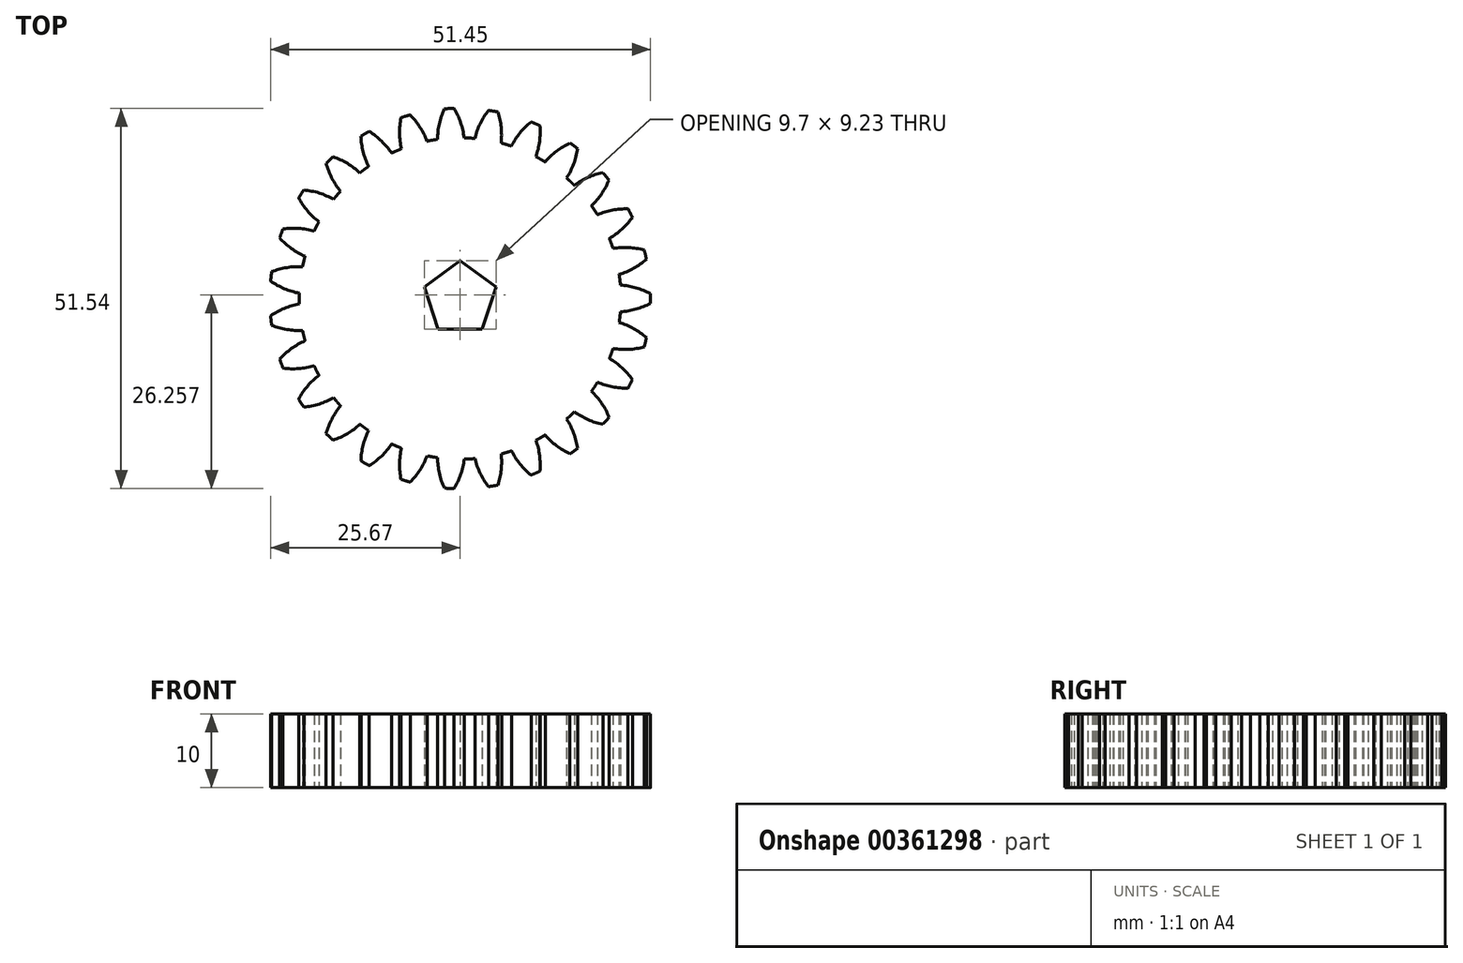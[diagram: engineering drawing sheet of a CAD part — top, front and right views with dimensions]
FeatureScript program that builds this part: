
annotation { "Feature Type Name" : "Feature", "Feature Type Description" : "" }
export const myFeature = defineFeature(function(context is Context, id is Id, definition is map)
    precondition{}
    {
        {
            var Q0;
            Q0=qCreatedBy(makeId("Top.planeOp"),FACE);
            var sketch = newSketch(context, id + "F0", { "sketchPlane" : qUnion([Q0])});
            skCircle(sketch, "E0", {"center": v(0, 0) * mm, "radius": 24 * mm, "construction": true});
            skArc(sketch, "E1", {"start": v(-3.07, 21.56) * mm, "mid": v(-3.42, 21.5) * mm, "end": v(-3.78, 21.45) * mm});
            skLineSegment(sketch, "E2", {"start": v(0, 0) * mm, "end": v(0, 48) * mm, "construction": true});
            skCircle(sketch, "E3", {"center": v(0, 48) * mm, "radius": 21.78 * mm, "construction": true});
            skCircle(sketch, "E4", {"center": v(0, 48) * mm, "radius": 24 * mm, "construction": true});
            skCircle(sketch, "E5", {"center": v(0, 48) * mm, "radius": 25.78 * mm, "construction": true});
            skLineSegment(sketch, "E6", {"start": v(0, 24) * mm, "end": v(46.56, 40.95) * mm, "construction": true});
            skLineSegment(sketch, "E7", {"start": v(0, 24) * mm, "end": v(-38.32, 10.05) * mm, "construction": true});
            skCircle(sketch, "E8", {"center": v(0, 48) * mm, "radius": 24.94 * mm, "construction": true});
            skCircle(sketch, "E9", {"center": v(0, 48) * mm, "radius": 23.14 * mm, "construction": true});
            skLineSegment(sketch, "E10", {"start": v(-4.02, 22.54) * mm, "end": v(-2.37, 18) * mm, "construction": true});
            skLineSegment(sketch, "E11", {"start": v(-2.3, 23.16) * mm, "end": v(-0.64, 18.6) * mm, "construction": true});
            skLineSegment(sketch, "E12", {"start": v(0, 24) * mm, "end": v(0.17, 23.53) * mm, "construction": true});
            skLineSegment(sketch, "E13", {"start": v(2.84, 25.03) * mm, "end": v(4.48, 20.5) * mm, "construction": true});
            skLineSegment(sketch, "E14", {"start": v(-4.02, 22.54) * mm, "end": v(0, 0) * mm, "construction": true});
            skLineSegment(sketch, "E15", {"start": v(0, 0) * mm, "end": v(-2.3, 23.16) * mm, "construction": true});
            skLineSegment(sketch, "E16", {"start": v(0, 0) * mm, "end": v(2.84, 25.03) * mm, "construction": true});
            skLineSegment(sketch, "E17.MirrorCS", {"start": v(0, 24) * mm, "end": v(38.32, 37.95) * mm, "construction": true});
            skLineSegment(sketch, "E18", {"start": v(0, 24) * mm, "end": v(-0.15, 24.42) * mm, "construction": true});
            skLineSegment(sketch, "E19", {"start": v(0.17, 23.53) * mm, "end": v(0, 0) * mm, "construction": true});
            skLineSegment(sketch, "E20", {"start": v(0, 0) * mm, "end": v(-0.15, 24.42) * mm, "construction": true});
            skLineSegment(sketch, "E21", {"start": v(-0.15, 24.42) * mm, "end": v(-0.7, 25.52) * mm, "construction": true});
            skLineSegment(sketch, "E22", {"start": v(0.17, 23.53) * mm, "end": v(0.42, 22.52) * mm, "construction": true});
            skLineSegment(sketch, "E23", {"start": v(0.42, 22.52) * mm, "end": v(0, 0) * mm, "construction": true});
            skLineSegment(sketch, "E24", {"start": v(0.42, 22.52) * mm, "end": v(0.86, 19.74) * mm, "construction": true});
            skLineSegment(sketch, "E25", {"start": v(0.42, 22.52) * mm, "end": v(0.54, 21.77) * mm, "construction": true});
            skLineSegment(sketch, "E26", {"start": v(0, 0) * mm, "end": v(-2.45, 41.99) * mm, "construction": true});
            skLineSegment(sketch, "E27", {"start": v(0, 0) * mm, "end": v(-4.95, 42.35) * mm, "construction": true});
            skLineSegment(sketch, "E28.MirrorCS", {"start": v(0, 0) * mm, "end": v(4.95, 42.35) * mm, "construction": true});
            skLineSegment(sketch, "E29.MirrorCS", {"start": v(0, 0) * mm, "end": v(2.45, 41.99) * mm, "construction": true});
            skArc(sketch, "E30.trimOffspring", {"start": v(0.54, 21.77) * mm, "mid": v(0.06, 23.84) * mm, "end": v(-0.86, 25.77) * mm});
            skArc(sketch, "E31.MirrorCS", {"start": v(-3.07, 21.56) * mm, "mid": v(-2.83, 23.68) * mm, "end": v(-2.15, 25.7) * mm});
            skLineSegment(sketch, "E32", {"start": v(0, 0) * mm, "end": v(-7.48, 42.4) * mm, "construction": true});
            skArc(sketch, "E33.trimOffspring", {"start": v(1.27, 21.74) * mm, "mid": v(0.9, 21.76) * mm, "end": v(0.54, 21.77) * mm});
            skArc(sketch, "E34.trimOffspring", {"start": v(-0.86, 25.77) * mm, "mid": v(-1.5, 25.74) * mm, "end": v(-2.15, 25.7) * mm});
            skArc(sketch, "E35.1.0", {"start": v(-7.96, 20.27) * mm, "mid": v(-8.3, 20.14) * mm, "end": v(-8.63, 20) * mm});
            skArc(sketch, "E35.1.1", {"start": v(-7.96, 20.27) * mm, "mid": v(-8.21, 22.39) * mm, "end": v(-8.01, 24.5) * mm});
            skArc(sketch, "E35.1.2", {"start": v(-6.77, 24.87) * mm, "mid": v(-7.4, 24.7) * mm, "end": v(-8.01, 24.5) * mm});
            skArc(sketch, "E35.1.3", {"start": v(-4.5, 21.31) * mm, "mid": v(-5.44, 23.21) * mm, "end": v(-6.77, 24.87) * mm});
            skArc(sketch, "E35.1.4", {"start": v(-3.78, 21.45) * mm, "mid": v(-4.14, 21.38) * mm, "end": v(-4.5, 21.31) * mm});
            skArc(sketch, "E35.2.0", {"start": v(-12.42, 17.9) * mm, "mid": v(-12.71, 17.68) * mm, "end": v(-13, 17.47) * mm});
            skArc(sketch, "E35.2.1", {"start": v(-12.42, 17.9) * mm, "mid": v(-13.15, 19.89) * mm, "end": v(-13.45, 22) * mm});
            skArc(sketch, "E35.2.2", {"start": v(-12.33, 22.64) * mm, "mid": v(-12.9, 22.32) * mm, "end": v(-13.45, 22) * mm});
            skArc(sketch, "E35.2.3", {"start": v(-9.3, 19.7) * mm, "mid": v(-10.65, 21.33) * mm, "end": v(-12.33, 22.64) * mm});
            skArc(sketch, "E35.2.4", {"start": v(-8.62, 20) * mm, "mid": v(-8.96, 19.85) * mm, "end": v(-9.3, 19.7) * mm});
            skArc(sketch, "E35.3.0", {"start": v(-16.2, 14.55) * mm, "mid": v(-16.45, 14.28) * mm, "end": v(-16.68, 14) * mm});
            skArc(sketch, "E35.3.1", {"start": v(-16.2, 14.55) * mm, "mid": v(-17.39, 16.32) * mm, "end": v(-18.16, 18.3) * mm});
            skArc(sketch, "E35.3.2", {"start": v(-17.22, 19.19) * mm, "mid": v(-17.7, 18.75) * mm, "end": v(-18.16, 18.3) * mm});
            skArc(sketch, "E35.3.3", {"start": v(-13.58, 17.02) * mm, "mid": v(-15.28, 18.3) * mm, "end": v(-17.22, 19.19) * mm});
            skArc(sketch, "E35.3.4", {"start": v(-13, 17.47) * mm, "mid": v(-13.3, 17.25) * mm, "end": v(-13.58, 17.02) * mm});
            skArc(sketch, "E35.4.0", {"start": v(-19.13, 10.42) * mm, "mid": v(-19.3, 10.1) * mm, "end": v(-19.46, 9.77) * mm});
            skArc(sketch, "E35.4.1", {"start": v(-19.13, 10.42) * mm, "mid": v(-20.68, 11.87) * mm, "end": v(-21.89, 13.62) * mm});
            skArc(sketch, "E35.4.2", {"start": v(-21.18, 14.7) * mm, "mid": v(-21.54, 14.16) * mm, "end": v(-21.89, 13.62) * mm});
            skArc(sketch, "E35.4.3", {"start": v(-17.14, 13.43) * mm, "mid": v(-19.1, 14.28) * mm, "end": v(-21.18, 14.7) * mm});
            skArc(sketch, "E35.4.4", {"start": v(-16.68, 14) * mm, "mid": v(-16.92, 13.72) * mm, "end": v(-17.14, 13.43) * mm});
            skArc(sketch, "E35.5.0", {"start": v(-21.01, 5.73) * mm, "mid": v(-21.1, 5.37) * mm, "end": v(-21.2, 5.02) * mm});
            skArc(sketch, "E35.5.1", {"start": v(-21.01, 5.73) * mm, "mid": v(-22.86, 6.78) * mm, "end": v(-24.44, 8.2) * mm});
            skArc(sketch, "E35.5.2", {"start": v(-24, 9.42) * mm, "mid": v(-24.23, 8.81) * mm, "end": v(-24.44, 8.2) * mm});
            skArc(sketch, "E35.5.3", {"start": v(-19.78, 9.12) * mm, "mid": v(-21.87, 9.5) * mm, "end": v(-24, 9.42) * mm});
            skArc(sketch, "E35.5.4", {"start": v(-19.46, 9.78) * mm, "mid": v(-19.62, 9.45) * mm, "end": v(-19.78, 9.12) * mm});
            skArc(sketch, "E35.6.0", {"start": v(-21.77, 0.72) * mm, "mid": v(-21.78, 0.36) * mm, "end": v(-21.78, 0) * mm});
            skArc(sketch, "E35.6.1", {"start": v(-21.77, 0.72) * mm, "mid": v(-23.8, 1.33) * mm, "end": v(-25.67, 2.35) * mm});
            skArc(sketch, "E35.6.2", {"start": v(-25.52, 3.63) * mm, "mid": v(-25.6, 2.99) * mm, "end": v(-25.67, 2.35) * mm});
            skArc(sketch, "E35.6.3", {"start": v(-21.35, 4.31) * mm, "mid": v(-23.47, 4.2) * mm, "end": v(-25.52, 3.63) * mm});
            skArc(sketch, "E35.6.4", {"start": v(-21.2, 5.03) * mm, "mid": v(-21.27, 4.67) * mm, "end": v(-21.35, 4.31) * mm});
            skArc(sketch, "E35.7.0", {"start": v(-21.35, -4.32) * mm, "mid": v(-21.27, -4.67) * mm, "end": v(-21.2, -5.02) * mm});
            skArc(sketch, "E35.7.1", {"start": v(-21.35, -4.32) * mm, "mid": v(-23.47, -4.2) * mm, "end": v(-25.52, -3.64) * mm});
            skArc(sketch, "E35.7.2", {"start": v(-25.67, -2.35) * mm, "mid": v(-25.6, -3) * mm, "end": v(-25.52, -3.64) * mm});
            skArc(sketch, "E35.7.3", {"start": v(-21.77, -0.73) * mm, "mid": v(-23.8, -1.33) * mm, "end": v(-25.67, -2.35) * mm});
            skArc(sketch, "E35.7.4", {"start": v(-21.78, 0) * mm, "mid": v(-21.78, -0.36) * mm, "end": v(-21.77, -0.73) * mm});
            skArc(sketch, "E35.8.0", {"start": v(-19.78, -9.12) * mm, "mid": v(-19.62, -9.45) * mm, "end": v(-19.46, -9.77) * mm});
            skArc(sketch, "E35.8.1", {"start": v(-19.78, -9.12) * mm, "mid": v(-21.87, -9.5) * mm, "end": v(-24, -9.43) * mm});
            skArc(sketch, "E35.8.2", {"start": v(-24.44, -8.2) * mm, "mid": v(-24.22, -8.82) * mm, "end": v(-24, -9.43) * mm});
            skArc(sketch, "E35.8.3", {"start": v(-21.01, -5.73) * mm, "mid": v(-22.86, -6.79) * mm, "end": v(-24.44, -8.2) * mm});
            skArc(sketch, "E35.8.4", {"start": v(-21.2, -5.02) * mm, "mid": v(-21.1, -5.38) * mm, "end": v(-21.01, -5.73) * mm});
            skArc(sketch, "E35.9.0", {"start": v(-17.14, -13.44) * mm, "mid": v(-16.92, -13.72) * mm, "end": v(-16.68, -14) * mm});
            skArc(sketch, "E35.9.1", {"start": v(-17.14, -13.44) * mm, "mid": v(-19.09, -14.29) * mm, "end": v(-21.17, -14.7) * mm});
            skArc(sketch, "E35.9.2", {"start": v(-21.89, -13.62) * mm, "mid": v(-21.54, -14.17) * mm, "end": v(-21.17, -14.7) * mm});
            skArc(sketch, "E35.9.3", {"start": v(-19.12, -10.42) * mm, "mid": v(-20.68, -11.87) * mm, "end": v(-21.89, -13.62) * mm});
            skArc(sketch, "E35.9.4", {"start": v(-19.46, -9.77) * mm, "mid": v(-19.3, -10.1) * mm, "end": v(-19.12, -10.42) * mm});
            skArc(sketch, "E35.10.0", {"start": v(-13.58, -17.03) * mm, "mid": v(-13.3, -17.25) * mm, "end": v(-13, -17.47) * mm});
            skArc(sketch, "E35.10.1", {"start": v(-13.58, -17.03) * mm, "mid": v(-15.28, -18.3) * mm, "end": v(-17.21, -19.2) * mm});
            skArc(sketch, "E35.10.2", {"start": v(-18.15, -18.3) * mm, "mid": v(-17.69, -18.75) * mm, "end": v(-17.21, -19.2) * mm});
            skArc(sketch, "E35.10.3", {"start": v(-16.2, -14.55) * mm, "mid": v(-17.38, -16.32) * mm, "end": v(-18.15, -18.3) * mm});
            skArc(sketch, "E35.10.4", {"start": v(-16.69, -14) * mm, "mid": v(-16.45, -14.28) * mm, "end": v(-16.2, -14.55) * mm});
            skArc(sketch, "E35.11.0", {"start": v(-9.29, -19.7) * mm, "mid": v(-8.96, -19.85) * mm, "end": v(-8.63, -20) * mm});
            skArc(sketch, "E35.11.1", {"start": v(-9.29, -19.7) * mm, "mid": v(-10.65, -21.34) * mm, "end": v(-12.32, -22.64) * mm});
            skArc(sketch, "E35.11.2", {"start": v(-13.44, -22) * mm, "mid": v(-12.89, -22.33) * mm, "end": v(-12.32, -22.64) * mm});
            skArc(sketch, "E35.11.3", {"start": v(-12.41, -17.9) * mm, "mid": v(-13.15, -19.9) * mm, "end": v(-13.44, -22) * mm});
            skArc(sketch, "E35.11.4", {"start": v(-13, -17.47) * mm, "mid": v(-12.71, -17.68) * mm, "end": v(-12.41, -17.9) * mm});
            skArc(sketch, "E35.12.0", {"start": v(-4.5, -21.31) * mm, "mid": v(-4.14, -21.38) * mm, "end": v(-3.78, -21.45) * mm});
            skArc(sketch, "E35.12.1", {"start": v(-4.5, -21.31) * mm, "mid": v(-5.44, -23.22) * mm, "end": v(-6.77, -24.88) * mm});
            skArc(sketch, "E35.12.2", {"start": v(-8, -24.5) * mm, "mid": v(-7.4, -24.7) * mm, "end": v(-6.77, -24.88) * mm});
            skArc(sketch, "E35.12.3", {"start": v(-7.95, -20.28) * mm, "mid": v(-8.2, -22.39) * mm, "end": v(-8, -24.5) * mm});
            skArc(sketch, "E35.12.4", {"start": v(-8.63, -20) * mm, "mid": v(-8.3, -20.14) * mm, "end": v(-7.95, -20.28) * mm});
            skArc(sketch, "E35.13.0", {"start": v(0.54, -21.77) * mm, "mid": v(0.9, -21.76) * mm, "end": v(1.27, -21.74) * mm});
            skArc(sketch, "E35.13.1", {"start": v(0.54, -21.77) * mm, "mid": v(0.06, -23.84) * mm, "end": v(-0.85, -25.77) * mm});
            skArc(sketch, "E35.13.2", {"start": v(-2.14, -25.7) * mm, "mid": v(-1.5, -25.74) * mm, "end": v(-0.85, -25.77) * mm});
            skArc(sketch, "E35.13.3", {"start": v(-3.06, -21.56) * mm, "mid": v(-2.82, -23.68) * mm, "end": v(-2.14, -25.7) * mm});
            skArc(sketch, "E35.13.4", {"start": v(-3.78, -21.45) * mm, "mid": v(-3.42, -21.5) * mm, "end": v(-3.06, -21.56) * mm});
            skArc(sketch, "E35.14.0", {"start": v(5.55, -21.06) * mm, "mid": v(5.9, -20.97) * mm, "end": v(6.25, -20.87) * mm});
            skArc(sketch, "E35.14.1", {"start": v(5.55, -21.06) * mm, "mid": v(5.56, -23.19) * mm, "end": v(5.12, -25.27) * mm});
            skArc(sketch, "E35.14.2", {"start": v(3.84, -25.5) * mm, "mid": v(4.48, -25.39) * mm, "end": v(5.12, -25.27) * mm});
            skArc(sketch, "E35.14.3", {"start": v(2, -21.69) * mm, "mid": v(2.71, -23.69) * mm, "end": v(3.84, -25.5) * mm});
            skArc(sketch, "E35.14.4", {"start": v(1.26, -21.74) * mm, "mid": v(1.63, -21.72) * mm, "end": v(2, -21.69) * mm});
            skArc(sketch, "E35.15.0", {"start": v(10.26, -19.21) * mm, "mid": v(10.57, -19.04) * mm, "end": v(10.9, -18.86) * mm});
            skArc(sketch, "E35.15.1", {"start": v(10.26, -19.21) * mm, "mid": v(10.76, -21.28) * mm, "end": v(10.8, -23.4) * mm});
            skArc(sketch, "E35.15.2", {"start": v(9.62, -23.92) * mm, "mid": v(10.21, -23.67) * mm, "end": v(10.8, -23.4) * mm});
            skArc(sketch, "E35.15.3", {"start": v(6.94, -20.64) * mm, "mid": v(8.1, -22.43) * mm, "end": v(9.62, -23.92) * mm});
            skArc(sketch, "E35.15.4", {"start": v(6.24, -20.87) * mm, "mid": v(6.6, -20.76) * mm, "end": v(6.94, -20.64) * mm});
            skArc(sketch, "E35.16.0", {"start": v(14.41, -16.33) * mm, "mid": v(14.68, -16.09) * mm, "end": v(14.95, -15.84) * mm});
            skArc(sketch, "E35.16.1", {"start": v(14.41, -16.33) * mm, "mid": v(15.37, -18.23) * mm, "end": v(15.91, -20.28) * mm});
            skArc(sketch, "E35.16.2", {"start": v(14.87, -21.06) * mm, "mid": v(15.4, -20.68) * mm, "end": v(15.91, -20.28) * mm});
            skArc(sketch, "E35.16.3", {"start": v(11.52, -18.49) * mm, "mid": v(13.06, -19.95) * mm, "end": v(14.87, -21.06) * mm});
            skArc(sketch, "E35.16.4", {"start": v(10.89, -18.86) * mm, "mid": v(11.2, -18.68) * mm, "end": v(11.52, -18.49) * mm});
            skArc(sketch, "E35.17.0", {"start": v(17.79, -12.57) * mm, "mid": v(18, -12.27) * mm, "end": v(18.2, -11.97) * mm});
            skArc(sketch, "E35.17.1", {"start": v(17.79, -12.57) * mm, "mid": v(19.16, -14.19) * mm, "end": v(20.16, -16.07) * mm});
            skArc(sketch, "E35.17.2", {"start": v(19.33, -17.06) * mm, "mid": v(19.75, -16.57) * mm, "end": v(20.16, -16.07) * mm});
            skArc(sketch, "E35.17.3", {"start": v(15.47, -15.33) * mm, "mid": v(17.3, -16.4) * mm, "end": v(19.33, -17.06) * mm});
            skArc(sketch, "E35.17.4", {"start": v(14.94, -15.84) * mm, "mid": v(15.2, -15.6) * mm, "end": v(15.47, -15.33) * mm});
            skArc(sketch, "E35.18.0", {"start": v(20.2, -8.13) * mm, "mid": v(20.34, -7.79) * mm, "end": v(20.47, -7.45) * mm});
            skArc(sketch, "E35.18.1", {"start": v(20.2, -8.13) * mm, "mid": v(21.92, -9.39) * mm, "end": v(23.32, -10.99) * mm});
            skArc(sketch, "E35.18.2", {"start": v(22.74, -12.14) * mm, "mid": v(23.04, -11.57) * mm, "end": v(23.32, -10.99) * mm});
            skArc(sketch, "E35.18.3", {"start": v(18.59, -11.35) * mm, "mid": v(20.62, -11.97) * mm, "end": v(22.74, -12.14) * mm});
            skArc(sketch, "E35.18.4", {"start": v(18.2, -11.97) * mm, "mid": v(18.4, -11.66) * mm, "end": v(18.59, -11.35) * mm});
            skArc(sketch, "E35.19.0", {"start": v(21.54, -3.25) * mm, "mid": v(21.59, -2.89) * mm, "end": v(21.63, -2.53) * mm});
            skArc(sketch, "E35.19.1", {"start": v(21.54, -3.25) * mm, "mid": v(23.5, -4.08) * mm, "end": v(25.23, -5.31) * mm});
            skArc(sketch, "E35.19.2", {"start": v(24.93, -6.57) * mm, "mid": v(25.09, -5.94) * mm, "end": v(25.23, -5.31) * mm});
            skArc(sketch, "E35.19.3", {"start": v(20.7, -6.76) * mm, "mid": v(22.83, -6.9) * mm, "end": v(24.93, -6.57) * mm});
            skArc(sketch, "E35.19.4", {"start": v(20.47, -7.45) * mm, "mid": v(20.59, -7.1) * mm, "end": v(20.7, -6.76) * mm});
            skArc(sketch, "E35.20.0", {"start": v(21.7, 1.8) * mm, "mid": v(21.67, 2.17) * mm, "end": v(21.63, 2.53) * mm});
            skArc(sketch, "E35.20.1", {"start": v(21.7, 1.8) * mm, "mid": v(23.8, 1.45) * mm, "end": v(25.77, 0.65) * mm});
            skArc(sketch, "E35.20.2", {"start": v(25.77, -0.64) * mm, "mid": v(25.78, 0) * mm, "end": v(25.77, 0.65) * mm});
            skArc(sketch, "E35.20.3", {"start": v(21.7, -1.8) * mm, "mid": v(23.8, -1.44) * mm, "end": v(25.77, -0.64) * mm});
            skArc(sketch, "E35.20.4", {"start": v(21.63, -2.53) * mm, "mid": v(21.67, -2.17) * mm, "end": v(21.7, -1.8) * mm});
            skArc(sketch, "E35.21.0", {"start": v(20.7, 6.76) * mm, "mid": v(20.59, 7.1) * mm, "end": v(20.47, 7.45) * mm});
            skArc(sketch, "E35.21.1", {"start": v(20.7, 6.76) * mm, "mid": v(22.83, 6.9) * mm, "end": v(24.93, 6.58) * mm});
            skArc(sketch, "E35.21.2", {"start": v(25.23, 5.32) * mm, "mid": v(25.08, 5.95) * mm, "end": v(24.93, 6.58) * mm});
            skArc(sketch, "E35.21.3", {"start": v(21.54, 3.25) * mm, "mid": v(23.5, 4.09) * mm, "end": v(25.23, 5.32) * mm});
            skArc(sketch, "E35.21.4", {"start": v(21.63, 2.53) * mm, "mid": v(21.59, 2.89) * mm, "end": v(21.54, 3.25) * mm});
            skArc(sketch, "E35.22.0", {"start": v(18.59, 11.36) * mm, "mid": v(18.4, 11.66) * mm, "end": v(18.2, 11.97) * mm});
            skArc(sketch, "E35.22.1", {"start": v(18.59, 11.36) * mm, "mid": v(20.62, 11.98) * mm, "end": v(22.74, 12.15) * mm});
            skArc(sketch, "E35.22.2", {"start": v(23.32, 11) * mm, "mid": v(23.04, 11.57) * mm, "end": v(22.74, 12.15) * mm});
            skArc(sketch, "E35.22.3", {"start": v(20.2, 8.13) * mm, "mid": v(21.92, 9.4) * mm, "end": v(23.32, 11) * mm});
            skArc(sketch, "E35.22.4", {"start": v(20.47, 7.45) * mm, "mid": v(20.34, 7.79) * mm, "end": v(20.2, 8.13) * mm});
            skArc(sketch, "E35.23.0", {"start": v(15.47, 15.34) * mm, "mid": v(15.2, 15.6) * mm, "end": v(14.95, 15.84) * mm});
            skArc(sketch, "E35.23.1", {"start": v(15.47, 15.34) * mm, "mid": v(17.3, 16.4) * mm, "end": v(19.32, 17.06) * mm});
            skArc(sketch, "E35.23.2", {"start": v(20.16, 16.07) * mm, "mid": v(19.75, 16.57) * mm, "end": v(19.32, 17.06) * mm});
            skArc(sketch, "E35.23.3", {"start": v(17.79, 12.57) * mm, "mid": v(19.16, 14.2) * mm, "end": v(20.16, 16.07) * mm});
            skArc(sketch, "E35.23.4", {"start": v(18.2, 11.97) * mm, "mid": v(18, 12.27) * mm, "end": v(17.79, 12.57) * mm});
            skArc(sketch, "E35.24.0", {"start": v(11.51, 18.49) * mm, "mid": v(11.2, 18.68) * mm, "end": v(10.89, 18.86) * mm});
            skArc(sketch, "E35.24.1", {"start": v(11.51, 18.49) * mm, "mid": v(13.05, 19.96) * mm, "end": v(14.87, 21.06) * mm});
            skArc(sketch, "E35.24.2", {"start": v(15.9, 20.29) * mm, "mid": v(15.4, 20.68) * mm, "end": v(14.87, 21.06) * mm});
            skArc(sketch, "E35.24.3", {"start": v(14.4, 16.33) * mm, "mid": v(15.37, 18.23) * mm, "end": v(15.9, 20.29) * mm});
            skArc(sketch, "E35.24.4", {"start": v(14.95, 15.84) * mm, "mid": v(14.68, 16.09) * mm, "end": v(14.4, 16.33) * mm});
            skArc(sketch, "E35.25.0", {"start": v(6.94, 20.65) * mm, "mid": v(6.6, 20.76) * mm, "end": v(6.25, 20.87) * mm});
            skArc(sketch, "E35.25.1", {"start": v(6.94, 20.65) * mm, "mid": v(8.1, 22.43) * mm, "end": v(9.61, 23.92) * mm});
            skArc(sketch, "E35.25.2", {"start": v(10.8, 23.4) * mm, "mid": v(10.2, 23.67) * mm, "end": v(9.61, 23.92) * mm});
            skArc(sketch, "E35.25.3", {"start": v(10.25, 19.22) * mm, "mid": v(10.75, 21.28) * mm, "end": v(10.8, 23.4) * mm});
            skArc(sketch, "E35.25.4", {"start": v(10.9, 18.86) * mm, "mid": v(10.57, 19.04) * mm, "end": v(10.25, 19.22) * mm});
            skArc(sketch, "E35.26.0", {"start": v(1.99, 21.69) * mm, "mid": v(1.63, 21.72) * mm, "end": v(1.27, 21.74) * mm});
            skArc(sketch, "E35.26.1", {"start": v(1.99, 21.69) * mm, "mid": v(2.7, 23.7) * mm, "end": v(3.83, 25.5) * mm});
            skArc(sketch, "E35.26.2", {"start": v(5.1, 25.27) * mm, "mid": v(4.47, 25.39) * mm, "end": v(3.83, 25.5) * mm});
            skArc(sketch, "E35.26.3", {"start": v(5.54, 21.06) * mm, "mid": v(5.55, 23.19) * mm, "end": v(5.1, 25.27) * mm});
            skArc(sketch, "E35.26.4", {"start": v(6.25, 20.86) * mm, "mid": v(5.9, 20.97) * mm, "end": v(5.54, 21.06) * mm});
            skLineSegment(sketch, "E36", {"start": v(0, 0) * mm, "end": v(-5.13, -5.13) * mm, "construction": true});
            skCircle(sketch, "E37", {"center": v(0, 0) * mm, "radius": 1 * mm});
            skCircle(sketch, "E38.cCircle", {"center": v(0, 0) * mm, "radius": 4.13 * mm, "construction": true});
            skLineSegment(sketch, "E38.0", {"start": v(4.85, 1.58) * mm, "end": v(3, -4.13) * mm});
            skLineSegment(sketch, "E38.1", {"start": v(3, -4.13) * mm, "end": v(-3, -4.13) * mm});
            skLineSegment(sketch, "E38.2", {"start": v(-3, -4.13) * mm, "end": v(-4.85, 1.58) * mm});
            skLineSegment(sketch, "E38.3", {"start": v(-4.85, 1.58) * mm, "end": v(0, 5.1) * mm});
            skLineSegment(sketch, "E38.4", {"start": v(0, 5.1) * mm, "end": v(4.85, 1.58) * mm});
            skSolve(sketch);
        }
        {
            var Q0;
            {var subQ41=sQuery(id+"F0.wireOp",EDGE,"E1");Q0=makeQuery(id+"F0.imprint","IMPRINT",FACE,{"disambiguationData":[TD([[makeQuery(id+"F0.imprint","IMPRINT",EDGE,{"derivedFrom":subQ41}),1.0]])]});}
            extrude(context, id + "F1", {"entities" : qUnion([Q0]), "depth" : 10 * mm});
        }
    });
